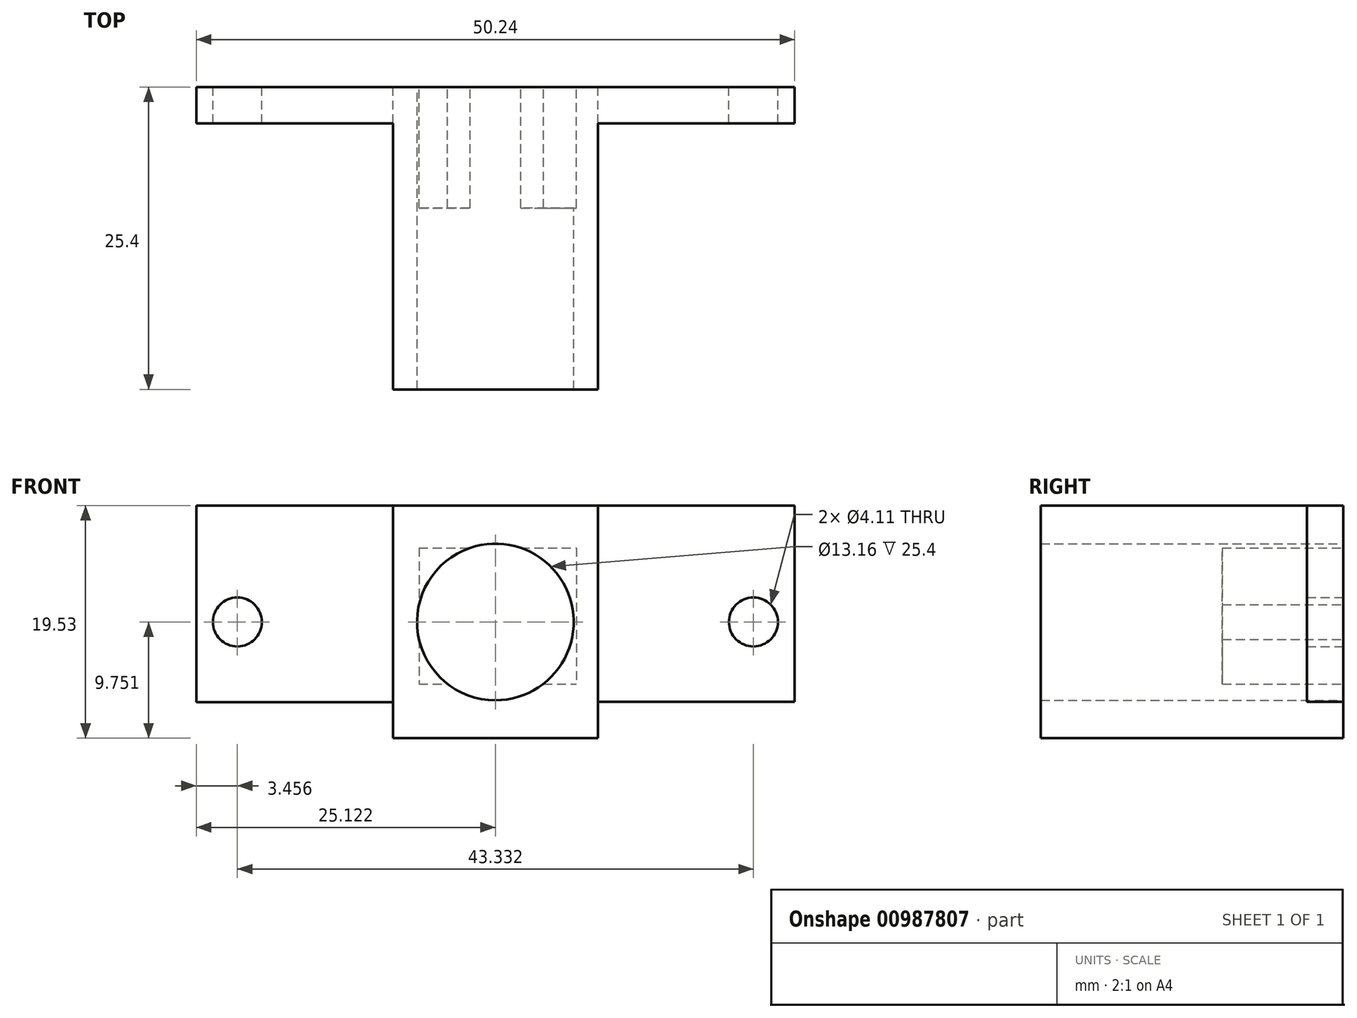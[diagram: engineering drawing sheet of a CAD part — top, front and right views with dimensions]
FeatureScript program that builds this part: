
annotation { "Feature Type Name" : "Feature", "Feature Type Description" : "" }
export const myFeature = defineFeature(function(context is Context, id is Id, definition is map)
    precondition{}
    {
        {
            var Q0;
            Q0=qCreatedBy(makeId("Front.planeOp"),FACE);
            var sketch = newSketch(context, id + "F0", { "sketchPlane" : qUnion([Q0])});
            skLineSegment(sketch, "E0", {"start": v(-40.83, 31.72) * mm, "end": v(-23.6, 31.72) * mm});
            skLineSegment(sketch, "E1", {"start": v(-40.83, 12.19) * mm, "end": v(-23.6, 12.19) * mm});
            skCircle(sketch, "E2", {"center": v(-32.22, 21.94) * mm, "radius": 6.58 * mm});
            skLineSegment(sketch, "E3", {"start": v(-40.83, 31.72) * mm, "end": v(-40.83, 12.19) * mm});
            skLineSegment(sketch, "E4", {"start": v(-23.6, 31.72) * mm, "end": v(-23.6, 12.19) * mm});
            skCircle(sketch, "E5", {"center": v(-32.22, 21.94) * mm, "radius": 2.06 * mm});
            skSolve(sketch);
        }
        {
            var Q0;
            Q0=makeQuery(id+"F0.imprint","IMPRINT",FACE,{"disambiguationData":[TD([[makeQuery(id+"F0.imprint","IMPRINT",EDGE,{"derivedFrom":sQuery(id+"F0.wireOp",EDGE,"SmfyHSjA-LpOb-Yx3U-Kuvu-dPIdQ33qvWrQ")}),-1.0]])]});
            var Q1;
            Q1=makeQuery(id+"F0.imprint","IMPRINT",FACE,{"disambiguationData":[TD([[makeQuery(id+"F0.imprint","IMPRINT",EDGE,{"derivedFrom":sQuery(id+"F0.wireOp",EDGE,"E0")}),-1.0]])]});
            extrude(context, id + "F1", {"entities" : qUnion([Q0, Q1]), "depth" : 25.4 * mm, "offsetDistance" : 25.4 * mm});
        }
        {
            var Q0;
            Q0=qCreatedBy(makeId("Front.planeOp"),FACE);
            var sketch = newSketch(context, id + "F2", { "sketchPlane" : qUnion([Q0])});
            skLineSegment(sketch, "E6", {"start": v(-40.83, 31.72) * mm, "end": v(-57.34, 31.72) * mm});
            skLineSegment(sketch, "E7", {"start": v(-40.83, 15.21) * mm, "end": v(-57.34, 15.21) * mm});
            skLineSegment(sketch, "E8", {"start": v(-57.34, 15.21) * mm, "end": v(-57.34, 31.72) * mm});
            skLineSegment(sketch, "E9", {"start": v(-23.6, 31.72) * mm, "end": v(-7.1, 31.72) * mm});
            skLineSegment(sketch, "E10", {"start": v(-8.37, 15.25) * mm, "end": v(-23.6, 15.25) * mm});
            skCircle(sketch, "E11", {"center": v(-53.88, 21.94) * mm, "radius": 2.06 * mm});
            skCircle(sketch, "E12", {"center": v(-10.55, 21.94) * mm, "radius": 2.06 * mm});
            skLineSegment(sketch, "E13", {"start": v(-23.6, 31.72) * mm, "end": v(-23.6, 15.25) * mm});
            skLineSegment(sketch, "E14", {"start": v(-40.83, 31.72) * mm, "end": v(-40.83, 15.21) * mm});
            skLineSegment(sketch, "E15.0", {"start": v(-23.6, 31.72) * mm, "end": v(-23.6, 12.19) * mm});
            skLineSegment(sketch, "E16", {"start": v(-8.37, 15.25) * mm, "end": v(-7.1, 15.25) * mm});
            skLineSegment(sketch, "E17", {"start": v(-7.1, 15.25) * mm, "end": v(-7.1, 31.76) * mm});
            skLineSegment(sketch, "E18", {"start": v(-7.1, 31.76) * mm, "end": v(-7.1, 31.72) * mm});
            skCircle(sketch, "E19.0", {"center": v(-32.22, 21.94) * mm, "radius": 2.06 * mm, "construction": true});
            skLineSegment(sketch, "E20", {"start": v(-32.22, 21.94) * mm, "end": v(-32.22, -5.98) * mm, "construction": true});
            skLineSegment(sketch, "E21", {"start": v(-10.55, 21.94) * mm, "end": v(-32.22, 21.94) * mm, "construction": true});
            skLineSegment(sketch, "E22", {"start": v(-32.22, 21.94) * mm, "end": v(-53.88, 21.94) * mm, "construction": true});
            skSolve(sketch);
        }
        {
            var Q0;
            Q0=makeQuery(id+"F2.imprint","IMPRINT",FACE,{"disambiguationData":[TD([[makeQuery(id+"F2.imprint","IMPRINT",EDGE,{"derivedFrom":sQuery(id+"F2.wireOp",EDGE,"E9")}),-1.0]])]});
            var Q1;
            Q1=makeQuery(id+"F2.imprint","IMPRINT",FACE,{"disambiguationData":[TD([[makeQuery(id+"F2.imprint","IMPRINT",EDGE,{"derivedFrom":sQuery(id+"F2.wireOp",EDGE,"E6")}),1.0]])]});
            extrude(context, id + "F3", {"entities" : qUnion([Q0, Q1]), "operationType" : NewBodyOperationType.ADD, "depth" : 3.05 * mm, "offsetDistance" : 25.4 * mm});
        }
        {
            var Q0;
            Q0=qCreatedBy(makeId("Front.planeOp"),FACE);
            var sketch = newSketch(context, id + "F4", { "sketchPlane" : qUnion([Q0])});
            skText(sketch, "E23", { "text": "R.P.U", "fontName": "OpenSans-Bold.ttf"});
            const initialGuessF4  = {"E23": [-0.03477, 0.02956, 1, 0, 0.00168]};
            skSetInitialGuess(sketch, initialGuessF4);
            skSolve(sketch);
        }
        {
            var Q0;
            Q0=qSketchRegion(id+"F4",true);
            extrude(context, id + "F5", {"entities" : qUnion([Q0]), "operationType" : NewBodyOperationType.ADD, "depth" : 22.86 * mm, "offsetDistance" : 25.4 * mm});
        }
        {
            var Q0;
            Q0=qCreatedBy(makeId("Front.planeOp"),FACE);
            var sketch = newSketch(context, id + "F6", { "sketchPlane" : qUnion([Q0])});
            skLineSegment(sketch, "E24", {"start": v(-38.63, 28.17) * mm, "end": v(-38.63, 16.74) * mm});
            skLineSegment(sketch, "E25", {"start": v(-38.63, 16.74) * mm, "end": v(-25.43, 16.74) * mm});
            skLineSegment(sketch, "E26", {"start": v(-38.63, 28.17) * mm, "end": v(-25.43, 28.17) * mm});
            skLineSegment(sketch, "E27", {"start": v(-25.43, 28.17) * mm, "end": v(-25.43, 16.74) * mm});
            skSolve(sketch);
        }
        {
            var Q0;
            Q0=makeQuery(id+"F6.imprint","IMPRINT",FACE,{"disambiguationData":[TD([[makeQuery(id+"F6.imprint","IMPRINT",EDGE,{"derivedFrom":sQuery(id+"F6.wireOp",EDGE,"E24")}),1.0]])]});
            extrude(context, id + "F7", {"entities" : qUnion([Q0]), "operationType" : NewBodyOperationType.REMOVE, "depth" : 10.16 * mm, "offsetDistance" : 25.4 * mm});
        }
    });
